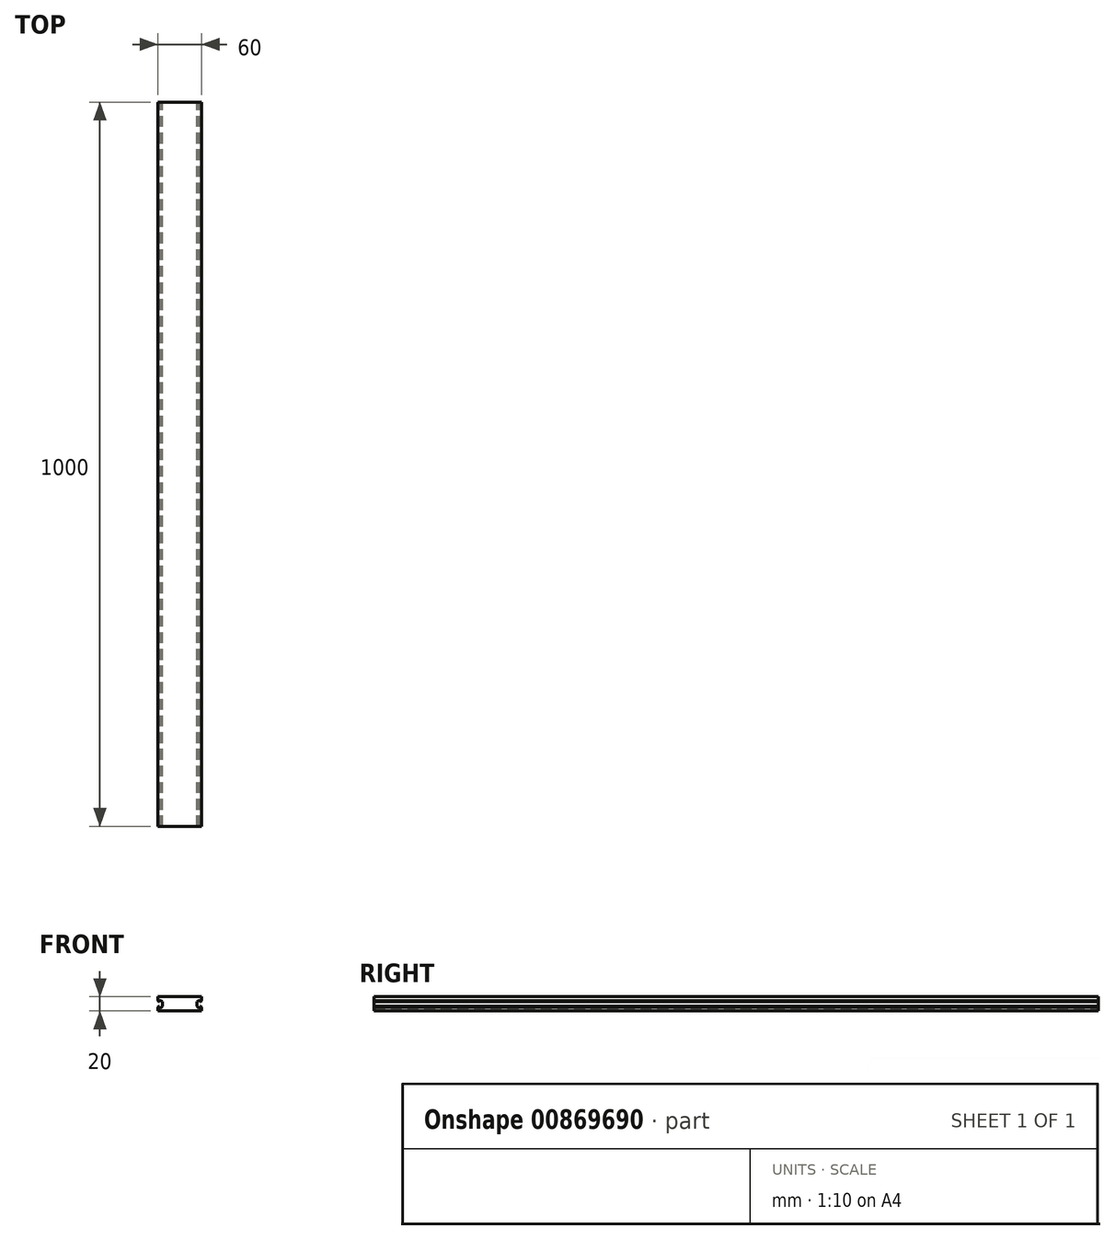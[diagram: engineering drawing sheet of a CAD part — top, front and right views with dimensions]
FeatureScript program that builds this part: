
annotation { "Feature Type Name" : "Feature", "Feature Type Description" : "" }
export const myFeature = defineFeature(function(context is Context, id is Id, definition is map)
    precondition{}
    {
        {
            var Q0;
            Q0=qCreatedBy(makeId("Front.planeOp"),FACE);
            var sketch = newSketch(context, id + "F0", { "sketchPlane" : qUnion([Q0])});
            skLineSegment(sketch, "E0", {"start": v(-30, 0) * mm, "end": v(-30, 5.5) * mm});
            skLineSegment(sketch, "E1", {"start": v(-30, 5.5) * mm, "end": v(-29, 6.9) * mm});
            skLineSegment(sketch, "E2", {"start": v(-29, 6.9) * mm, "end": v(-28.2, 6.9) * mm});
            skLineSegment(sketch, "E3", {"start": v(-28.2, 6.9) * mm, "end": v(-28.2, 4.3) * mm});
            skLineSegment(sketch, "E4", {"start": v(-28.2, 4.3) * mm, "end": v(-26.4, 4.3) * mm});
            skLineSegment(sketch, "E5", {"start": v(-26.4, 4.3) * mm, "end": v(-23.85, 6.9) * mm});
            skLineSegment(sketch, "E6", {"start": v(-23.85, 6.9) * mm, "end": v(-23.85, 13.1) * mm});
            skLineSegment(sketch, "E7", {"start": v(-23.85, 13.1) * mm, "end": v(-26.4, 14.5) * mm});
            skLineSegment(sketch, "E8", {"start": v(-26.4, 14.5) * mm, "end": v(-28.2, 14.5) * mm});
            skLineSegment(sketch, "E9", {"start": v(-28.2, 14.5) * mm, "end": v(-28.2, 13.1) * mm});
            skLineSegment(sketch, "E10", {"start": v(-28.2, 13.1) * mm, "end": v(-29, 13.1) * mm});
            skLineSegment(sketch, "E11", {"start": v(-29, 13.1) * mm, "end": v(-30, 14.5) * mm});
            skLineSegment(sketch, "E12", {"start": v(-30, 14.5) * mm, "end": v(-30, 20) * mm});
            skLineSegment(sketch, "E13", {"start": v(-30, 20) * mm, "end": v(0, 20) * mm});
            skLineSegment(sketch, "E14", {"start": v(-30, 0) * mm, "end": v(0, 0) * mm});
            skLineSegment(sketch, "E15", {"start": v(0, 47.06) * mm, "end": v(0, -36.89) * mm});
            skLineSegment(sketch, "E16.MirrorCS", {"start": v(30, 20) * mm, "end": v(0, 20) * mm});
            skLineSegment(sketch, "E17.MirrorCS", {"start": v(30, 14.5) * mm, "end": v(30, 20) * mm});
            skLineSegment(sketch, "E18.MirrorCS", {"start": v(29, 13.1) * mm, "end": v(30, 14.5) * mm});
            skLineSegment(sketch, "E19.MirrorCS", {"start": v(28.2, 13.1) * mm, "end": v(29, 13.1) * mm});
            skLineSegment(sketch, "E20.MirrorCS", {"start": v(28.2, 14.5) * mm, "end": v(28.2, 13.1) * mm});
            skLineSegment(sketch, "E21.MirrorCS", {"start": v(26.4, 14.5) * mm, "end": v(28.2, 14.5) * mm});
            skLineSegment(sketch, "E22.MirrorCS", {"start": v(23.85, 13.1) * mm, "end": v(26.4, 14.5) * mm});
            skLineSegment(sketch, "E23.MirrorCS", {"start": v(23.85, 6.9) * mm, "end": v(23.85, 13.1) * mm});
            skLineSegment(sketch, "E24.MirrorCS", {"start": v(26.4, 4.3) * mm, "end": v(23.85, 6.9) * mm});
            skLineSegment(sketch, "E25.MirrorCS", {"start": v(28.2, 4.3) * mm, "end": v(26.4, 4.3) * mm});
            skLineSegment(sketch, "E26.MirrorCS", {"start": v(28.2, 6.9) * mm, "end": v(28.2, 4.3) * mm});
            skLineSegment(sketch, "E27.MirrorCS", {"start": v(29, 6.9) * mm, "end": v(28.2, 6.9) * mm});
            skLineSegment(sketch, "E28.MirrorCS", {"start": v(30, 5.5) * mm, "end": v(29, 6.9) * mm});
            skLineSegment(sketch, "E29.MirrorCS", {"start": v(30, 0) * mm, "end": v(30, 5.5) * mm});
            skLineSegment(sketch, "E30.MirrorCS", {"start": v(30, 0) * mm, "end": v(0, 0) * mm});
            skSolve(sketch);
        }
        {
            var Q0;
            Q0 = qSketchRegion(id + "F0", true);
            extrude(context, id + "F1", {"entities" : qUnion([Q0]), "depth" : 1000 * mm, "offsetDistance" : 25 * mm});
        }
    });
